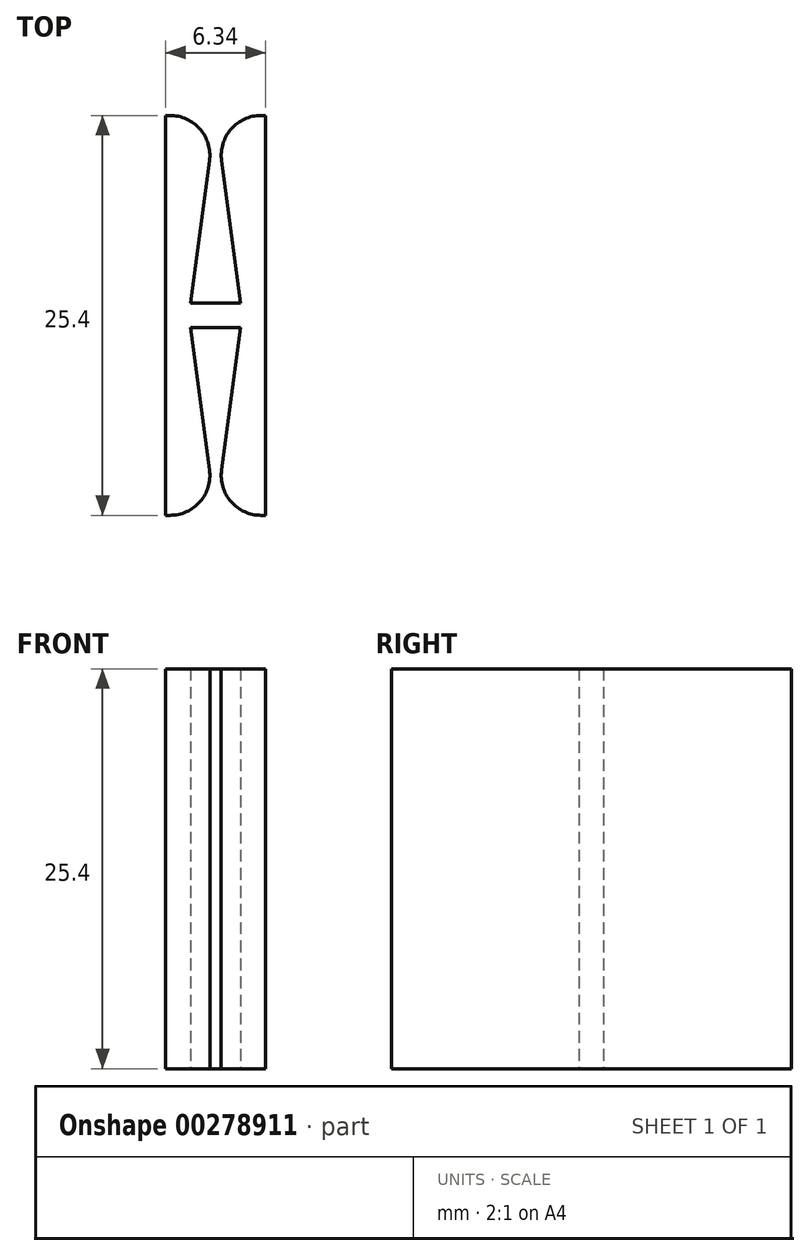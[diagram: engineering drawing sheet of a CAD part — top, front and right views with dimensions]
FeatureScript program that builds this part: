
annotation { "Feature Type Name" : "Feature", "Feature Type Description" : "" }
export const myFeature = defineFeature(function(context is Context, id is Id, definition is map)
    precondition{}
    {
        {
            var Q0;
            Q0=qCreatedBy(makeId("Top.planeOp"),FACE);
            var sketch = newSketch(context, id + "F0", { "sketchPlane" : qUnion([Q0])});
            skLineSegment(sketch, "E0.bottom", {"start": v(-20.22, -14.71) * mm, "end": v(-19.95, -14.71) * mm});
            skLineSegment(sketch, "E0.top", {"start": v(-20.22, -40.11) * mm, "end": v(-19.95, -40.11) * mm});
            skLineSegment(sketch, "E0.left", {"start": v(-20.22, -14.71) * mm, "end": v(-20.22, -40.11) * mm});
            skLineSegment(sketch, "E0.right", {"start": v(-13.88, -14.71) * mm, "end": v(-13.88, -40.11) * mm});
            skLineSegment(sketch, "E1.top", {"start": v(-18.64, -26.64) * mm, "end": v(-15.46, -26.64) * mm});
            skLineSegment(sketch, "E1.left", {"start": v(-17.43, -17.59) * mm, "end": v(-18.64, -26.64) * mm});
            skLineSegment(sketch, "E1.right", {"start": v(-16.67, -17.59) * mm, "end": v(-15.46, -26.64) * mm});
            skLineSegment(sketch, "E2.top", {"start": v(-18.64, -28.2) * mm, "end": v(-15.46, -28.2) * mm});
            skLineSegment(sketch, "E2.left", {"start": v(-17.43, -37.24) * mm, "end": v(-18.64, -28.2) * mm});
            skLineSegment(sketch, "E2.right", {"start": v(-16.67, -37.24) * mm, "end": v(-15.46, -28.2) * mm});
            skLineSegment(sketch, "E3.trimOffspring", {"start": v(-14.15, -14.71) * mm, "end": v(-13.88, -14.71) * mm});
            skLineSegment(sketch, "E4.trimOffspring", {"start": v(-14.15, -40.11) * mm, "end": v(-13.88, -40.11) * mm});
            skPoint(sketch, "E5", {"position": v(-13.88, -28.2) * mm});
            skPoint(sketch, "E6", {"position": v(-20.22, -28.2) * mm});
            skLineSegment(sketch, "E7", {"start": v(-20.22, -28.2) * mm, "end": v(-18.64, -28.2) * mm});
            skLineSegment(sketch, "E8", {"start": v(-15.46, -28.2) * mm, "end": v(-13.88, -28.2) * mm});
            skPoint(sketch, "E9.visualSharp", {"position": v(-17.05, -14.71) * mm});
            skArc(sketch, "E9.filletArc", {"start": v(-17.43, -17.59) * mm, "mid": v(-18.04, -15.58) * mm, "end": v(-19.95, -14.71) * mm});
            skArc(sketch, "E10.filletArc", {"start": v(-14.15, -14.71) * mm, "mid": v(-16.06, -15.58) * mm, "end": v(-16.67, -17.59) * mm});
            skPoint(sketch, "E11.visualSharp", {"position": v(-17.05, -40.11) * mm});
            skArc(sketch, "E11.filletArc", {"start": v(-19.95, -40.11) * mm, "mid": v(-18.04, -39.25) * mm, "end": v(-17.43, -37.24) * mm});
            skArc(sketch, "E12.filletArc", {"start": v(-16.67, -37.24) * mm, "mid": v(-16.06, -39.25) * mm, "end": v(-14.15, -40.11) * mm});
            skPoint(sketch, "E13", {"position": v(-13.88, -27.41) * mm});
            skLineSegment(sketch, "E14", {"start": v(-13.88, -27.41) * mm, "end": v(-20.22, -27.41) * mm, "construction": true});
            skLineSegment(sketch, "E15", {"start": v(-18.64, -26.64) * mm, "end": v(-15.46, -28.2) * mm, "construction": true});
            skLineSegment(sketch, "E16", {"start": v(-18.64, -28.2) * mm, "end": v(-15.46, -26.64) * mm, "construction": true});
            skPoint(sketch, "E17", {"position": v(-17.05, -27.41) * mm});
            skSolve(sketch);
        }
        {
            var Q0;
            {var subQ3=sQuery(id+"F0.wireOp",EDGE,"E0.bottom");Q0=makeQuery(id+"F0.imprint","IMPRINT",FACE,{"disambiguationData":[TD([[makeQuery(id+"F0.imprint","IMPRINT",EDGE,{"derivedFrom":subQ3}),-1.0]])]});}
            var Q1;
            {var subQ2=sQuery(id+"F0.wireOp",EDGE,"E0.top");Q1=makeQuery(id+"F0.imprint","IMPRINT",FACE,{"disambiguationData":[TD([[makeQuery(id+"F0.imprint","IMPRINT",EDGE,{"derivedFrom":subQ2}),1.0]])]});}
            var Q2;
            Q2=makeQuery(id+"F0.imprint","IMPRINT",FACE,{"disambiguationData":[TD([[makeQuery(id+"F0.imprint","IMPRINT",EDGE,{"derivedFrom":sQuery(id+"F0.wireOp",EDGE,"E2.right")}),-1.0]])]});
            extrude(context, id + "F1", {"entities" : qUnion([Q0, Q1, Q2]), "depth" : 25.4 * mm});
        }
    });
